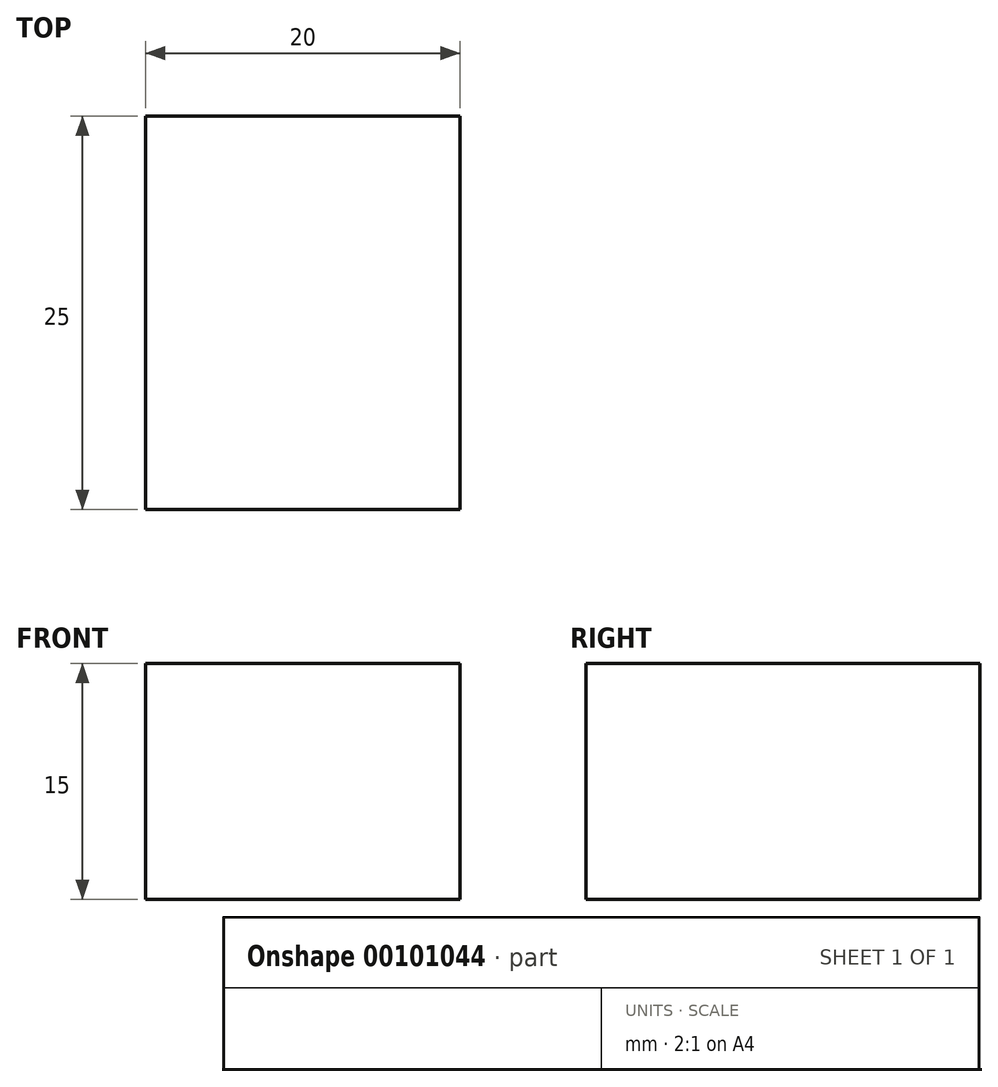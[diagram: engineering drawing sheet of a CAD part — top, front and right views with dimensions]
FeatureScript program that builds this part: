
annotation { "Feature Type Name" : "Feature", "Feature Type Description" : "" }
export const myFeature = defineFeature(function(context is Context, id is Id, definition is map)
    precondition{}
    {
        {
            var Q0;
            Q0=qCreatedBy(makeId("Front.planeOp"),FACE);
            var sketch = newSketch(context, id + "F0", { "sketchPlane" : qUnion([Q0])});
            skLineSegment(sketch, "E0.bottom", {"start": v(0, 0) * mm, "end": v(20, 0) * mm});
            skLineSegment(sketch, "E0.top", {"start": v(0, 15) * mm, "end": v(20, 15) * mm});
            skLineSegment(sketch, "E0.left", {"start": v(0, 0) * mm, "end": v(0, 15) * mm});
            skLineSegment(sketch, "E0.right", {"start": v(20, 0) * mm, "end": v(20, 15) * mm});
            skSolve(sketch);
        }
        {
            var Q0;
            Q0 = qSketchRegion(id + "F0", true);
            extrude(context, id + "F1", {"entities" : qUnion([Q0]), "depth" : 25 * mm});
        }
    });
